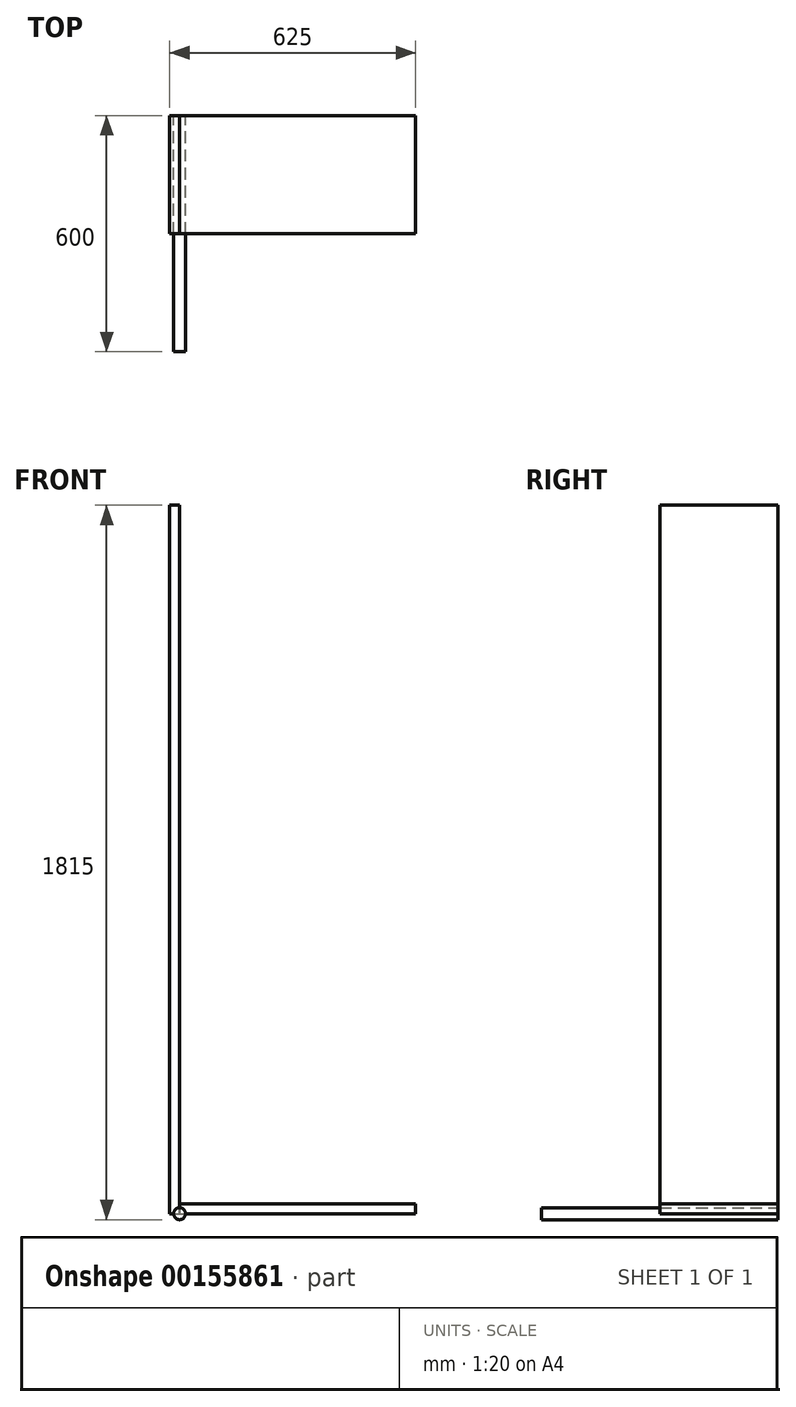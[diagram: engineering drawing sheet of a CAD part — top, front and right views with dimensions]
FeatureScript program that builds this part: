
annotation { "Feature Type Name" : "Feature", "Feature Type Description" : "" }
export const myFeature = defineFeature(function(context is Context, id is Id, definition is map)
    precondition{}
    {
        {
            var Q0;
            Q0=qCreatedBy(makeId("Top.planeOp"),FACE);
            var sketch = newSketch(context, id + "F0", { "sketchPlane" : qUnion([Q0])});
            skLineSegment(sketch, "E0.bottom", {"start": v(0, 0) * mm, "end": v(600, 0) * mm});
            skLineSegment(sketch, "E0.top", {"start": v(0, -300) * mm, "end": v(600, -300) * mm});
            skLineSegment(sketch, "E0.left", {"start": v(0, 0) * mm, "end": v(0, -300) * mm});
            skLineSegment(sketch, "E0.right", {"start": v(600, 0) * mm, "end": v(600, -300) * mm});
            skSolve(sketch);
        }
        {
            var Q0;
            Q0 = qSketchRegion(id + "F0", true);
            extrude(context, id + "F1", {"entities" : qUnion([Q0]), "depth" : 25 * mm});
        }
        {
            var Q0;
            Q0=qCreatedBy(makeId("Right.planeOp"),FACE);
            var sketch = newSketch(context, id + "F2", { "sketchPlane" : qUnion([Q0])});
            skLineSegment(sketch, "E1.bottom", {"start": v(0, 0) * mm, "end": v(-300, 0) * mm});
            skLineSegment(sketch, "E1.top", {"start": v(0, 1800) * mm, "end": v(-300, 1800) * mm});
            skLineSegment(sketch, "E1.left", {"start": v(0, 0) * mm, "end": v(0, 1800) * mm});
            skLineSegment(sketch, "E1.right", {"start": v(-300, 0) * mm, "end": v(-300, 1800) * mm});
            skSolve(sketch);
        }
        {
            var Q0;
            Q0 = qSketchRegion(id + "F2", true);
            extrude(context, id + "F3", {"entities" : qUnion([Q0]), "oppositeDirection" : true, "depth" : 25 * mm});
        }
        {
            var Q0;
            Q0=qCreatedBy(makeId("Front.planeOp"),FACE);
            var sketch = newSketch(context, id + "F4", { "sketchPlane" : qUnion([Q0])});
            skCircle(sketch, "E2", {"center": v(0, 0) * mm, "radius": 15 * mm});
            skSolve(sketch);
        }
        {
            var Q0;
            Q0 = qSketchRegion(id + "F4", true);
            extrude(context, id + "F5", {"entities" : qUnion([Q0]), "depth" : 600 * mm});
        }
    });
